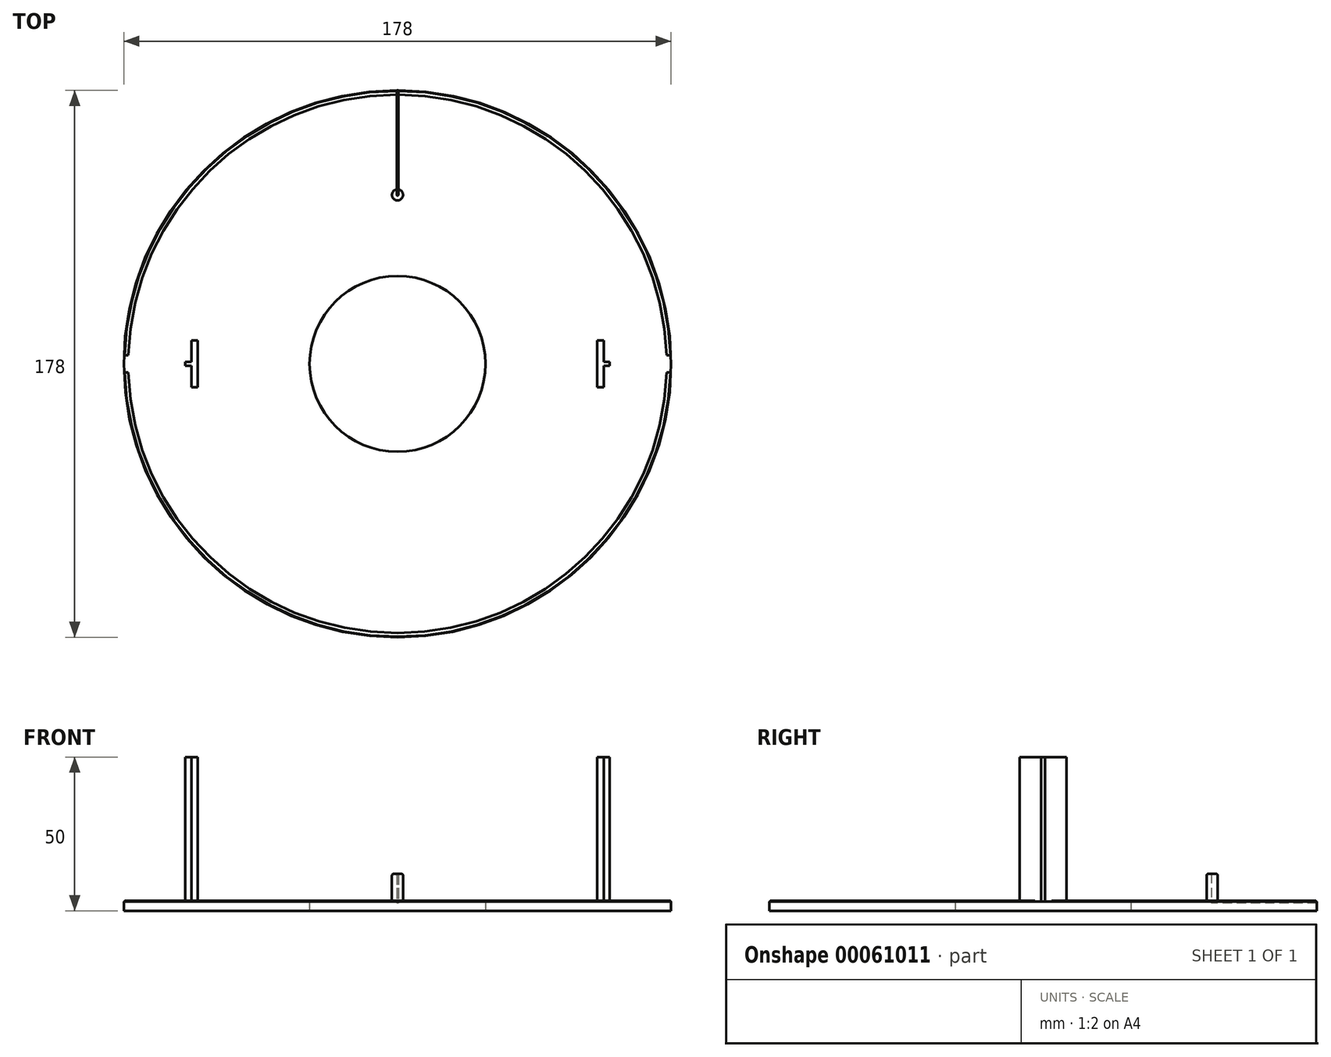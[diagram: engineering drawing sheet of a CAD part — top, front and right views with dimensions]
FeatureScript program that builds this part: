
annotation { "Feature Type Name" : "Feature", "Feature Type Description" : "" }
export const myFeature = defineFeature(function(context is Context, id is Id, definition is map)
    precondition{}
    {
        {
            var Q0;
            Q0=qCreatedBy(makeId("Top.planeOp"),FACE);
            var sketch = newSketch(context, id + "F0", { "sketchPlane" : qUnion([Q0])});
            skCircle(sketch, "E0", {"center": v(0, 0) * mm, "radius": 89 * mm});
            skCircle(sketch, "E1", {"center": v(0, 0) * mm, "radius": 28.6 * mm});
            skSolve(sketch);
        }
        {
            var Q0;
            Q0=makeQuery(id+"F0.imprint","IMPRINT",FACE,{"disambiguationData":[TD([[makeQuery(id+"F0.imprint","IMPRINT",EDGE,{"derivedFrom":sQuery(id+"F0.wireOp",EDGE,"E0")}),1.0]])]});
            extrude(context, id + "F1", {"entities" : qUnion([Q0]), "depth" : 3 * mm});
        }
        {
            var Q0;
            Q0=makeQuery(id+"F1.opExtrude","CAP_FACE",FACE,{"disambiguationData":[OSD([sQuery(id+"F0.wireOp",EDGE,"E0"),sQuery(id+"F0.wireOp",EDGE,"E1")])],"isStart":false});
            var sketch = newSketch(context, id + "F2", { "sketchPlane" : qUnion([Q0])});
            skLineSegment(sketch, "E2", {"start": v(-89, 0) * mm, "end": v(89, 0) * mm, "construction": true});
            skLineSegment(sketch, "E3.bottom", {"start": v(-67.05, 7.65) * mm, "end": v(-64.95, 7.65) * mm});
            skLineSegment(sketch, "E3.top", {"start": v(-67.05, -7.65) * mm, "end": v(-64.95, -7.65) * mm});
            skLineSegment(sketch, "E3.left", {"start": v(-67.05, 7.65) * mm, "end": v(-67.05, 0.65) * mm});
            skLineSegment(sketch, "E3.right", {"start": v(-64.95, 7.65) * mm, "end": v(-64.95, -7.65) * mm});
            skLineSegment(sketch, "E4", {"start": v(-67.05, 0.65) * mm, "end": v(-69.05, 0.65) * mm});
            skLineSegment(sketch, "E5", {"start": v(-69.05, 0.65) * mm, "end": v(-69.05, -0.65) * mm});
            skLineSegment(sketch, "E6", {"start": v(-69.05, -0.65) * mm, "end": v(-67.05, -0.65) * mm});
            skPoint(sketch, "E7", {"position": v(-69.05, 0) * mm});
            skPoint(sketch, "E8", {"position": v(-64.95, 0) * mm});
            skPoint(sketch, "E9", {"position": v(-66, -7.65) * mm});
            skPoint(sketch, "E10", {"position": v(-66, 7.65) * mm});
            skLineSegment(sketch, "E11", {"start": v(-66, 7.65) * mm, "end": v(-66, -7.65) * mm, "construction": true});
            skLineSegment(sketch, "E12.trimOffspring", {"start": v(-67.05, -0.65) * mm, "end": v(-67.05, -7.65) * mm});
            skSolve(sketch);
        }
        {
            var Q0;
            Q0=makeQuery(id+"F2.imprint","IMPRINT",FACE,{"disambiguationData":[TD([[makeQuery(id+"F2.imprint","IMPRINT",EDGE,{"derivedFrom":sQuery(id+"F2.wireOp",EDGE,"E3.bottom")}),-1.0]])]});
            extrude(context, id + "F3", {"entities" : qUnion([Q0]), "operationType" : NewBodyOperationType.ADD, "depth" : 47 * mm});
        }
        {
            var Q0;
            Q0=makeQuery(id+"F1.opExtrude","SWEPT_BODY",BODY,{"disambiguationData":[OSD([sQuery(id+"F0.wireOp",EDGE,"E0"),sQuery(id+"F0.wireOp",EDGE,"E1")])]});
            var Q1;
            Q1=qCreatedBy(makeId("Right.planeOp"),FACE);
            mirror(context, id + "F4", {"operationType" : NewBodyOperationType.ADD, "entities" : qUnion([Q0]), "mirrorPlane" : qUnion([Q1])});
        }
        {
            var Q0;
            Q0=makeQuery(id+"F1.opExtrude","CAP_FACE",FACE,{"disambiguationData":[OSD([sQuery(id+"F0.wireOp",EDGE,"E0"),sQuery(id+"F0.wireOp",EDGE,"E1")])],"isStart":false});
            var sketch = newSketch(context, id + "F5", { "sketchPlane" : qUnion([Q0])});
            skLineSegment(sketch, "E13", {"start": v(0, 0) * mm, "end": v(0, 89) * mm, "construction": true});
            skArc(sketch, "E14", {"start": v(-0.25, 56.78) * mm, "mid": v(0, 53.2) * mm, "end": v(0.25, 56.78) * mm});
            skLineSegment(sketch, "E15", {"start": v(-0.25, 56.78) * mm, "end": v(-0.25, 55) * mm});
            skLineSegment(sketch, "E16", {"start": v(0.25, 55) * mm, "end": v(0.25, 56.78) * mm});
            skArc(sketch, "E17", {"start": v(-0.25, 55) * mm, "mid": v(0, 54.75) * mm, "end": v(0.25, 55) * mm});
            skSolve(sketch);
        }
        {
            var Q0;
            Q0=makeQuery(id+"F5.imprint","IMPRINT",FACE,{"disambiguationData":[TD([[makeQuery(id+"F5.imprint","IMPRINT",EDGE,{"derivedFrom":sQuery(id+"F5.wireOp",EDGE,"E14")}),1.0]])]});
            extrude(context, id + "F6", {"entities" : qUnion([Q0]), "operationType" : NewBodyOperationType.ADD, "depth" : 9 * mm});
        }
        {
            var Q0;
            Q0=makeQuery(id+"F6.opExtrude","CAP_EDGE",EDGE,{"disambiguationData":[OSD([sQuery(id+"F5.wireOp",EDGE,"E14")])],"isStart":false});
            fillet(context, id + "F7", {"entities" : qUnion([Q0]), "radius" : 0.5 * mm, "tangentPropagation" : true, "allowEdgeOverflow" : false});
        }
        {
            var Q0;
            Q0=makeQuery(id+"F1.opExtrude","CAP_FACE",FACE,{"disambiguationData":[OSD([sQuery(id+"F0.wireOp",EDGE,"E0"),sQuery(id+"F0.wireOp",EDGE,"E1")])],"isStart":false});
            var sketch = newSketch(context, id + "F8", { "sketchPlane" : qUnion([Q0])});
            skArc(sketch, "E18.0", {"start": v(88.76, 2.75) * mm, "mid": v(0, 88.8) * mm, "end": v(-88.76, 2.75) * mm});
            skArc(sketch, "E19.0", {"start": v(87.56, 2.75) * mm, "mid": v(0, 87.6) * mm, "end": v(-87.56, 2.75) * mm});
            skLineSegment(sketch, "E20.bottom", {"start": v(87.56, 2.75) * mm, "end": v(88.76, 2.75) * mm});
            skLineSegment(sketch, "E20.top", {"start": v(87.56, -2.75) * mm, "end": v(88.76, -2.75) * mm});
            skLineSegment(sketch, "E20.left", {"start": v(87.56, 2.75) * mm, "end": v(87.56, -2.75) * mm, "construction": true});
            skLineSegment(sketch, "E20.right", {"start": v(88.76, 2.75) * mm, "end": v(88.76, -2.75) * mm, "construction": true});
            skLineSegment(sketch, "E21", {"start": v(0, 0) * mm, "end": v(87.56, 0) * mm, "construction": true});
            skLineSegment(sketch, "E22.bottom", {"start": v(-88.76, 2.75) * mm, "end": v(-87.56, 2.75) * mm});
            skLineSegment(sketch, "E22.top", {"start": v(-88.76, -2.75) * mm, "end": v(-87.56, -2.75) * mm});
            skLineSegment(sketch, "E22.left", {"start": v(-88.76, 2.75) * mm, "end": v(-88.76, -2.75) * mm, "construction": true});
            skLineSegment(sketch, "E22.right", {"start": v(-87.56, 2.75) * mm, "end": v(-87.56, -2.75) * mm, "construction": true});
            skLineSegment(sketch, "E23", {"start": v(0, 0) * mm, "end": v(-87.56, 0) * mm, "construction": true});
            skArc(sketch, "E24.trimOffspring", {"start": v(-87.56, -2.75) * mm, "mid": v(0, -87.6) * mm, "end": v(87.56, -2.75) * mm});
            skArc(sketch, "E25.trimOffspring", {"start": v(-88.76, -2.75) * mm, "mid": v(0, -88.8) * mm, "end": v(88.76, -2.75) * mm});
            skSolve(sketch);
        }
        {
            var Q0;
            Q0=makeQuery(id+"F8.imprint","IMPRINT",FACE,{"disambiguationData":[TD([[makeQuery(id+"F8.imprint","IMPRINT",EDGE,{"derivedFrom":sQuery(id+"F8.wireOp",EDGE,"E18.0")}),1.0]])]});
            var Q1;
            Q1=makeQuery(id+"F8.imprint","IMPRINT",FACE,{"disambiguationData":[TD([[makeQuery(id+"F8.imprint","IMPRINT",EDGE,{"derivedFrom":sQuery(id+"F8.wireOp",EDGE,"E20.top")}),-1.0]])]});
            extrude(context, id + "F9", {"entities" : qUnion([Q0, Q1]), "operationType" : NewBodyOperationType.ADD, "depth" : 0.2 * mm});
        }
        {
            var Q0;
            Q0=makeQuery(id+"F6.opExtrude","CAP_FACE",FACE,{"disambiguationData":[OSD([sQuery(id+"F5.wireOp",EDGE,"E14"),sQuery(id+"F5.wireOp",EDGE,"E15"),sQuery(id+"F5.wireOp",EDGE,"E16"),sQuery(id+"F5.wireOp",EDGE,"E17")])],"isStart":false});
            var sketch = newSketch(context, id + "F10", { "sketchPlane" : qUnion([Q0])});
            skLineSegment(sketch, "E26", {"start": v(0.25, 56.28) * mm, "end": v(0.25, 92) * mm});
            skLineSegment(sketch, "E27", {"start": v(0.25, 92) * mm, "end": v(-0.25, 92) * mm});
            skLineSegment(sketch, "E28", {"start": v(-0.25, 92) * mm, "end": v(-0.25, 56.28) * mm});
            skSolve(sketch);
        }
        {
            var Q0;
            Q0=makeQuery(id+"F10.imprint","IMPRINT",FACE,{"disambiguationData":[TD([[makeQuery(id+"F10.imprint","IMPRINT",EDGE,{"derivedFrom":sQuery(id+"F10.wireOp",EDGE,"E26")}),1.0]])]});
            extrude(context, id + "F11", {"entities" : qUnion([Q0]), "operationType" : NewBodyOperationType.REMOVE, "oppositeDirection" : true, "depth" : 9.5 * mm});
        }
    });
